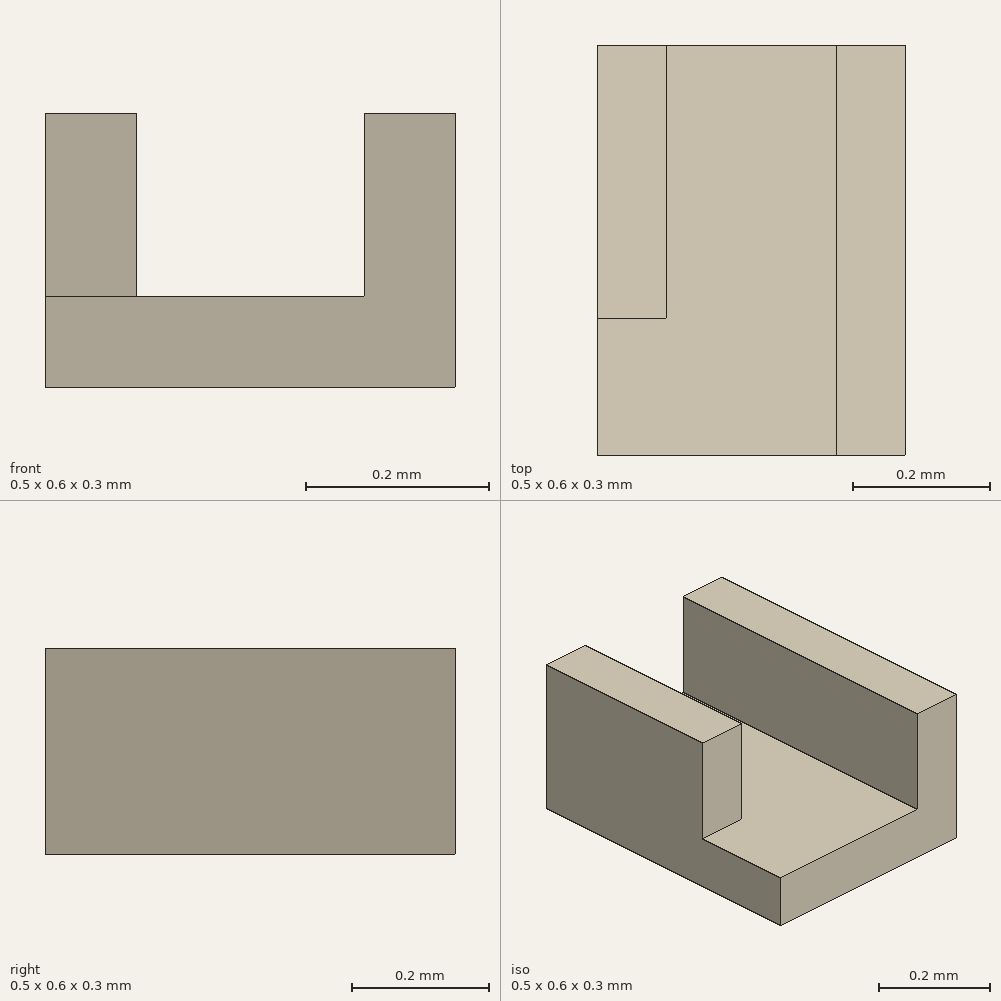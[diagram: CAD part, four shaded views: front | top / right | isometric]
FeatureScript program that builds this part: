
annotation { "Feature Type Name" : "Feature", "Feature Type Description" : "" }
export const myFeature = defineFeature(function(context is Context, id is Id, definition is map)
    precondition{}
    {
        {
            var Q0;
            Q0=qCreatedBy(makeId("Front.planeOp"),FACE);
            var sketch = newSketch(context, id + "F0", { "sketchPlane" : qUnion([Q0])});
            skLineSegment(sketch, "E0.bottom", {"start": v(0.23, 0.15) * mm, "end": v(0.12, 0.15) * mm});
            skLineSegment(sketch, "E0.top", {"start": v(0.23, -0.15) * mm, "end": v(-0.23, -0.15) * mm});
            skLineSegment(sketch, "E0.left", {"start": v(0.23, 0.15) * mm, "end": v(0.23, -0.15) * mm});
            skLineSegment(sketch, "E0.right", {"start": v(-0.22, 0.15) * mm, "end": v(-0.23, -0.15) * mm});
            skPoint(sketch, "E0.middle", {"position": v(0, 0) * mm});
            skLineSegment(sketch, "E1", {"start": v(0.12, 0.15) * mm, "end": v(0.12, -0.05) * mm});
            skLineSegment(sketch, "E2.top", {"start": v(0.13, -0.05) * mm, "end": v(-0.12, -0.05) * mm});
            skLineSegment(sketch, "E2.right", {"start": v(-0.12, 0.15) * mm, "end": v(-0.12, -0.05) * mm});
            skLineSegment(sketch, "E3.trimOffspring", {"start": v(-0.12, 0.15) * mm, "end": v(-0.22, 0.15) * mm});
            skSolve(sketch);
        }
        {
            var Q0;
            Q0=makeQuery(id+"F0.imprint","IMPRINT",FACE,{"disambiguationData":[TD([[makeQuery(id+"F0.imprint","IMPRINT",EDGE,{"derivedFrom":sQuery(id+"F0.wireOp",EDGE,"E0.bottom")}),1.0]])]});
            extrude(context, id + "F1", {"entities" : qUnion([Q0]), "depth" : 0.6 * mm});
        }
        {
            var Q0;
            Q0=makeQuery(id+"F1.opExtrude","SWEPT_FACE",FACE,{"disambiguationData":[OSD([sQuery(id+"F0.wireOp",EDGE,"E0.right")])]});
            var sketch = newSketch(context, id + "F2", { "sketchPlane" : qUnion([Q0])});
            skLineSegment(sketch, "E4.bottom", {"start": v(0.6, 0.15) * mm, "end": v(0.4, 0.15) * mm});
            skLineSegment(sketch, "E4.top", {"start": v(0.6, -0.05) * mm, "end": v(0.4, -0.05) * mm});
            skLineSegment(sketch, "E4.left", {"start": v(0.6, 0.15) * mm, "end": v(0.6, -0.05) * mm});
            skLineSegment(sketch, "E4.right", {"start": v(0.4, 0.15) * mm, "end": v(0.4, -0.05) * mm});
            skSolve(sketch);
        }
        {
            var Q0;
            Q0=makeQuery(id+"F2.imprint","IMPRINT",FACE,{"disambiguationData":[TD([[makeQuery(id+"F2.imprint","IMPRINT",EDGE,{"derivedFrom":sQuery(id+"F2.wireOp",EDGE,"E4.bottom")}),1.0]])]});
            extrude(context, id + "F3", {"entities" : qUnion([Q0]), "operationType" : NewBodyOperationType.REMOVE, "oppositeDirection" : true, "depth" : 0.2 * mm});
        }
    });
